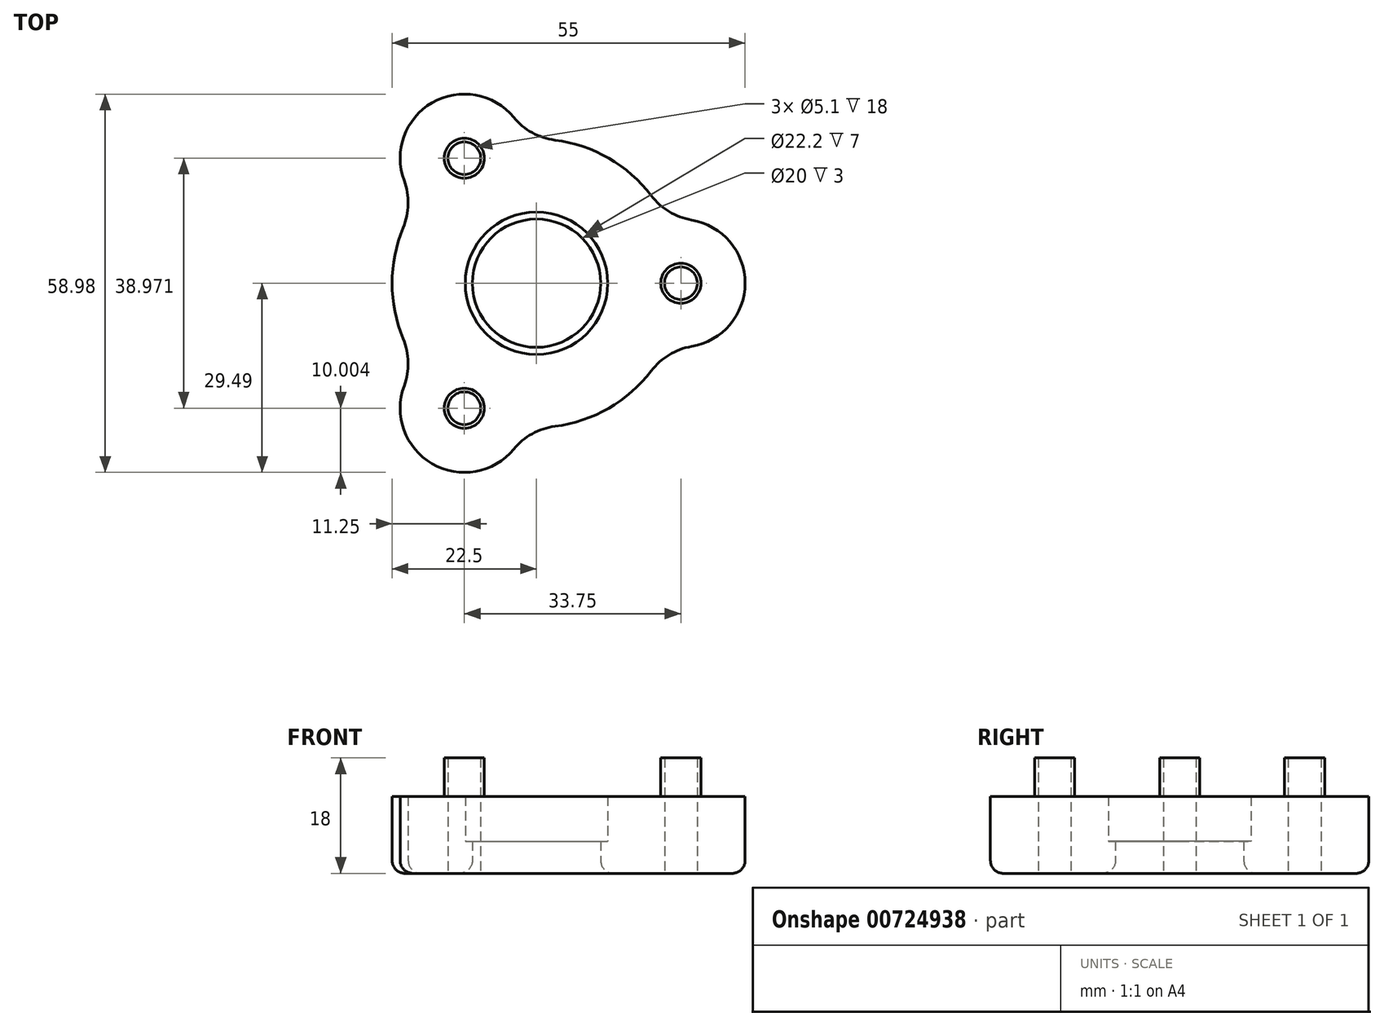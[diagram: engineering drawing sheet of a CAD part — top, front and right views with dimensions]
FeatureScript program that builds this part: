
annotation { "Feature Type Name" : "Feature", "Feature Type Description" : "" }
export const myFeature = defineFeature(function(context is Context, id is Id, definition is map)
    precondition{}
    {
        {
            var Q0;
            Q0=qCreatedBy(makeId("Top.planeOp"),FACE);
            var sketch = newSketch(context, id + "F0", { "sketchPlane" : qUnion([Q0])});
            skCircle(sketch, "E0", {"center": v(0, 0) * mm, "radius": 11.1 * mm});
            skArc(sketch, "E1", {"start": v(-8.97, 20.63) * mm, "mid": v(-11.25, 19.49) * mm, "end": v(-13.38, 18.09) * mm});
            skCircle(sketch, "E2", {"center": v(22.5, 0) * mm, "radius": 2.55 * mm});
            skArc(sketch, "E3", {"start": v(24.17, -9.86) * mm, "mid": v(32.5, 0) * mm, "end": v(24.17, 9.86) * mm});
            skArc(sketch, "E4.1.0", {"start": v(-3.54, 25.86) * mm, "mid": v(-16.25, 28.15) * mm, "end": v(-20.62, 16) * mm});
            skCircle(sketch, "E4.1.1", {"center": v(-11.25, 19.49) * mm, "radius": 2.55 * mm});
            skArc(sketch, "E4.2.0", {"start": v(-20.62, -16) * mm, "mid": v(-16.25, -28.15) * mm, "end": v(-3.54, -25.86) * mm});
            skCircle(sketch, "E4.2.1", {"center": v(-11.25, -19.49) * mm, "radius": 2.55 * mm});
            skArc(sketch, "E5.trimOffspring", {"start": v(-20.77, 8.66) * mm, "mid": v(-22.5, 0) * mm, "end": v(-20.77, -8.66) * mm});
            skArc(sketch, "E6.trimOffspring", {"start": v(2.88, -22.31) * mm, "mid": v(11.25, -19.49) * mm, "end": v(17.88, -13.65) * mm});
            skArc(sketch, "E7.trimOffspring", {"start": v(17.88, 13.65) * mm, "mid": v(11.25, 19.49) * mm, "end": v(2.88, 22.31) * mm});
            skPoint(sketch, "E8.visualSharp", {"position": v(20.28, 9.75) * mm});
            skArc(sketch, "E8.filletArc", {"start": v(17.88, 13.65) * mm, "mid": v(20.67, 11.16) * mm, "end": v(24.17, 9.86) * mm});
            skPoint(sketch, "E9.visualSharp", {"position": v(-1.7, 22.44) * mm});
            skArc(sketch, "E9.filletArc", {"start": v(-3.54, 25.86) * mm, "mid": v(-0.67, 23.48) * mm, "end": v(2.88, 22.31) * mm});
            skPoint(sketch, "E10.visualSharp", {"position": v(-18.58, 12.69) * mm});
            skArc(sketch, "E10.filletArc", {"start": v(-20.77, 8.66) * mm, "mid": v(-20, 12.32) * mm, "end": v(-20.62, 16) * mm});
            skPoint(sketch, "E11.visualSharp", {"position": v(-18.58, -12.69) * mm});
            skArc(sketch, "E11.filletArc", {"start": v(-20.62, -16) * mm, "mid": v(-20, -12.32) * mm, "end": v(-20.77, -8.66) * mm});
            skPoint(sketch, "E12.visualSharp", {"position": v(-1.7, -22.44) * mm});
            skArc(sketch, "E12.filletArc", {"start": v(2.88, -22.31) * mm, "mid": v(-0.67, -23.48) * mm, "end": v(-3.54, -25.86) * mm});
            skPoint(sketch, "E13.visualSharp", {"position": v(20.28, -9.75) * mm});
            skArc(sketch, "E13.filletArc", {"start": v(24.17, -9.86) * mm, "mid": v(20.67, -11.16) * mm, "end": v(17.88, -13.65) * mm});
            skSolve(sketch);
        }
        {
            var Q0;
            Q0=makeQuery(id+"F0.imprint","IMPRINT",FACE,{"disambiguationData":[TD([[makeQuery(id+"F0.imprint","IMPRINT",EDGE,{"derivedFrom":sQuery(id+"F0.wireOp",EDGE,"E0")}),-1.0]])]});
            extrude(context, id + "F1", {"entities" : qUnion([Q0]), "depth" : 12 * mm, "offsetDistance" : 25 * mm});
        }
        {
            var Q0;
            Q0=makeQuery(id+"F1.opExtrude","CAP_FACE",FACE,{"disambiguationData":[OSD([sQuery(id+"F0.wireOp",EDGE,"E0"),sQuery(id+"F0.wireOp",EDGE,"E2"),sQuery(id+"F0.wireOp",EDGE,"E3"),sQuery(id+"F0.wireOp",EDGE,"E4.1.0"),sQuery(id+"F0.wireOp",EDGE,"E4.1.1"),sQuery(id+"F0.wireOp",EDGE,"E4.2.0"),sQuery(id+"F0.wireOp",EDGE,"E4.2.1"),sQuery(id+"F0.wireOp",EDGE,"E5.trimOffspring"),sQuery(id+"F0.wireOp",EDGE,"E6.trimOffspring"),sQuery(id+"F0.wireOp",EDGE,"E7.trimOffspring"),sQuery(id+"F0.wireOp",EDGE,"E8.filletArc"),sQuery(id+"F0.wireOp",EDGE,"E9.filletArc"),sQuery(id+"F0.wireOp",EDGE,"E10.filletArc"),sQuery(id+"F0.wireOp",EDGE,"E11.filletArc"),sQuery(id+"F0.wireOp",EDGE,"E12.filletArc"),sQuery(id+"F0.wireOp",EDGE,"E13.filletArc")])],"isStart":true});
            var sketch = newSketch(context, id + "F2", { "sketchPlane" : qUnion([Q0])});
            skCircle(sketch, "E14", {"center": v(0, 0) * mm, "radius": 10 * mm});
            skCircle(sketch, "E15", {"center": v(0, 0) * mm, "radius": 11.5 * mm});
            skSolve(sketch);
        }
        {
            var Q0;
            Q0 = qSketchRegion(id + "F2", true);
            extrude(context, id + "F3", {"entities" : qUnion([Q0]), "operationType" : NewBodyOperationType.ADD, "oppositeDirection" : true, "depth" : 5 * mm, "offsetDistance" : 25 * mm});
        }
        {
            var Q0;
            Q0=makeQuery(id+"F1.opExtrude","CAP_FACE",FACE,{"disambiguationData":[OSD([sQuery(id+"F0.wireOp",EDGE,"E0"),sQuery(id+"F0.wireOp",EDGE,"E2"),sQuery(id+"F0.wireOp",EDGE,"E3"),sQuery(id+"F0.wireOp",EDGE,"E4.1.0"),sQuery(id+"F0.wireOp",EDGE,"E4.1.1"),sQuery(id+"F0.wireOp",EDGE,"E4.2.0"),sQuery(id+"F0.wireOp",EDGE,"E4.2.1"),sQuery(id+"F0.wireOp",EDGE,"E5.trimOffspring"),sQuery(id+"F0.wireOp",EDGE,"E6.trimOffspring"),sQuery(id+"F0.wireOp",EDGE,"E7.trimOffspring"),sQuery(id+"F0.wireOp",EDGE,"E8.filletArc"),sQuery(id+"F0.wireOp",EDGE,"E9.filletArc"),sQuery(id+"F0.wireOp",EDGE,"E10.filletArc"),sQuery(id+"F0.wireOp",EDGE,"E11.filletArc"),sQuery(id+"F0.wireOp",EDGE,"E12.filletArc"),sQuery(id+"F0.wireOp",EDGE,"E13.filletArc")])],"isStart":false});
            var sketch = newSketch(context, id + "F4", { "sketchPlane" : qUnion([Q0])});
            skCircle(sketch, "E16", {"center": v(-11.25, 19.49) * mm, "radius": 2.55 * mm});
            skCircle(sketch, "E17", {"center": v(-11.25, 19.49) * mm, "radius": 3.12 * mm});
            skCircle(sketch, "E18", {"center": v(22.5, 0) * mm, "radius": 2.55 * mm});
            skCircle(sketch, "E19", {"center": v(22.5, 0) * mm, "radius": 3.12 * mm});
            skCircle(sketch, "E20", {"center": v(-11.25, -19.49) * mm, "radius": 2.55 * mm});
            skCircle(sketch, "E21", {"center": v(-11.25, -19.49) * mm, "radius": 3.12 * mm});
            skSolve(sketch);
        }
        {
            var Q0;
            Q0 = qSketchRegion(id + "F4", true);
            extrude(context, id + "F5", {"entities" : qUnion([Q0]), "operationType" : NewBodyOperationType.ADD, "depth" : 6 * mm, "offsetDistance" : 25 * mm});
        }
        {
            var Q0;
            Q0=makeQuery(id+"F1.opExtrude","CAP_EDGE",EDGE,{"disambiguationData":[OSD([sQuery(id+"F0.wireOp",EDGE,"E6.trimOffspring")])],"isStart":true});
            var Q1;
            Q1=makeQuery(id+"F3.opExtrude","CAP_EDGE",EDGE,{"disambiguationData":[OSD([sQuery(id+"F2.wireOp",EDGE,"E14")])],"isStart":true});
            fillet(context, id + "F6", {"entities" : qUnion([Q0, Q1]), "radius" : 2 * mm, "tangentPropagation" : true, "allowEdgeOverflow" : false});
        }
    });
